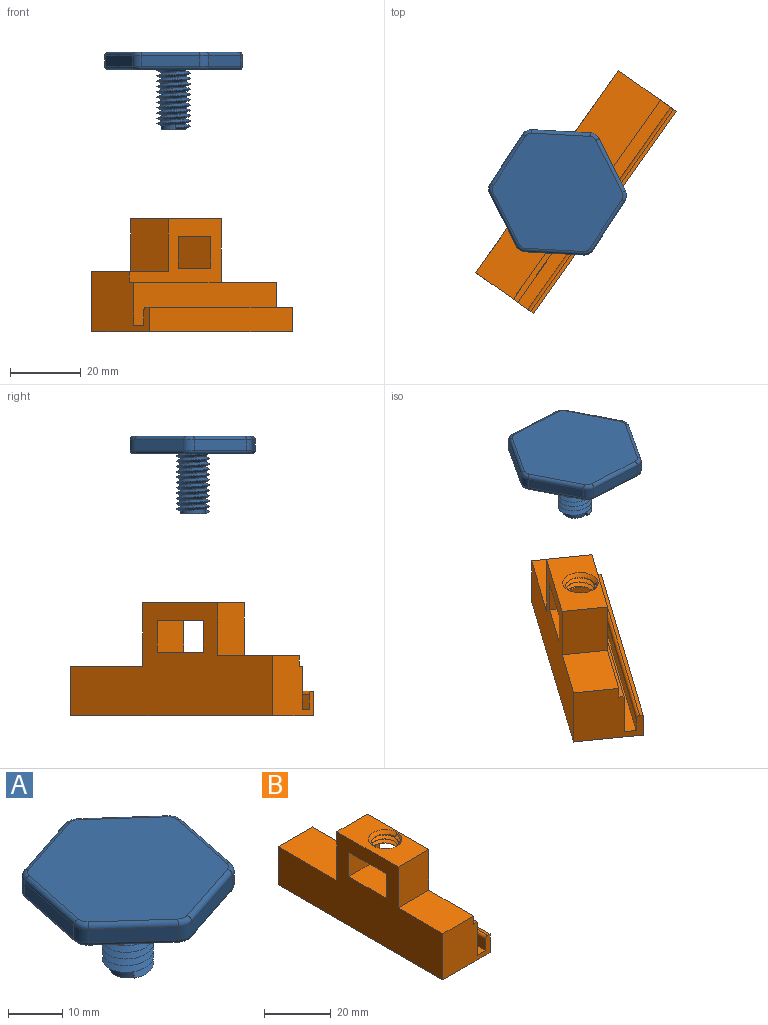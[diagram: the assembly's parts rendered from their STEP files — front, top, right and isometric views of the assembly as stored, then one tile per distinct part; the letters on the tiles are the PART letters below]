
ASSEMBLY  parts=2 mates=1
PART A: 43 faces, bbox 38.8x39.8x22.9 mm
  f0: plane 37.3x36.33mm, normal (0,0,-1), area 869mm2, adj f2,f3,f4,f13,f14,f15,f16,f17
  f1: plane 36.38x35.41mm, normal (0,0,1), area 921.4mm2, adj f19,f20,f21,f22,f23,f24,f27,f30
  f2: cylinder r=3.5mm len=17mm, axis (0,0,-1), area 1.1mm2, adj f0,f3,f4,f5,f6
  f3: bspline ~17.2x10.88mm, area 384.8mm2, adj f0,f2,f4,f6
  f4: bspline ~17.95x10.88mm, area 401.1mm2, adj f0,f2,f3,f6
  f5: plane 7x7mm, normal (0,0,-1), area 38.5mm2, adj f2
  f6: plane 1.4x1.05mm, normal (-0.87,0.5,0), area 0.8mm2, adj f2,f3,f4
  f7: plane 12.34x11.01mm, normal (-0.67,-0.75,0), area 49.6mm2, adj f15,f21,f38,f41
  f8: plane 15.71x5.18mm, normal (0.31,-0.95,0), area 49.6mm2, adj f13,f19,f35,f38
  f9: plane 16.19x3.37mm, normal (0.98,-0.2,0), area 49.6mm2, adj f14,f20,f32,f35
  f10: plane 12.34x11.01mm, normal (0.67,0.75,0), area 49.6mm2, adj f16,f22,f26,f32
  f11: plane 15.71x5.18mm, normal (-0.31,0.95,0), area 49.6mm2, adj f18,f24,f26,f29
  f12: plane 16.19x3.37mm, normal (-0.98,0.2,0), area 49.6mm2, adj f17,f23,f29,f41
  f13: cylinder r=1mm len=16.02mm, axis (-0.95,-0.31,0), area 26mm2, adj f0,f8,f34,f37
  f14: cylinder r=1mm len=16.39mm, axis (-0.2,-0.98,0), area 26mm2, adj f0,f9,f31,f34
  f15: cylinder r=1mm len=13mm, axis (-0.75,0.67,0), area 26mm2, adj f0,f7,f37,f40
  f16: cylinder r=1mm len=13mm, axis (0.75,-0.67,0), area 26mm2, adj f0,f10,f25,f31
  f17: cylinder r=1mm len=16.39mm, axis (0.2,0.98,0), area 26mm2, adj f0,f12,f28,f40
  f18: cylinder r=1mm len=16.02mm, axis (0.95,0.31,0), area 26mm2, adj f0,f11,f25,f28
  f19: cylinder r=1mm len=16.02mm, axis (0.95,0.31,0), area 26mm2, adj f1,f8,f36,f39
  f20: cylinder r=1mm len=16.39mm, axis (0.2,0.98,0), area 26mm2, adj f1,f9,f33,f36
  f21: cylinder r=1mm len=13mm, axis (0.75,-0.67,0), area 26mm2, adj f1,f7,f39,f42
  f22: cylinder r=1mm len=13mm, axis (-0.75,0.67,0), area 26mm2, adj f1,f10,f27,f33
  f23: cylinder r=1mm len=16.39mm, axis (-0.2,-0.98,0), area 26mm2, adj f1,f12,f30,f42
  f24: cylinder r=1mm len=16.02mm, axis (-0.95,-0.31,0), area 26mm2, adj f1,f11,f27,f30
  f25: torus R=2mm, axis (0,0,1), area 4.3mm2, adj f0,f16,f18,f26
  f26: cylinder r=3mm len=3mm, axis (0,0,1), area 9.4mm2, adj f10,f11,f25,f27
  f27: torus R=2mm, axis (0,0,1), area 4.3mm2, adj f1,f22,f24,f26
  f28: torus R=2mm, axis (0,0,1), area 4.3mm2, adj f0,f17,f18,f29
  f29: cylinder r=3mm len=3mm, axis (0,0,1), area 9.4mm2, adj f11,f12,f28,f30
  f30: torus R=2mm, axis (0,0,1), area 4.3mm2, adj f1,f23,f24,f29
  f31: torus R=2mm, axis (0,0,1), area 4.3mm2, adj f0,f14,f16,f32
  f32: cylinder r=3mm len=3mm, axis (0,0,1), area 9.4mm2, adj f9,f10,f31,f33
  f33: torus R=2mm, axis (0,0,1), area 4.3mm2, adj f1,f20,f22,f32
  f34: torus R=2mm, axis (0,0,1), area 4.3mm2, adj f0,f13,f14,f35
  f35: cylinder r=3mm len=3mm, axis (0,0,1), area 9.4mm2, adj f8,f9,f34,f36
  f36: torus R=2mm, axis (0,0,1), area 4.3mm2, adj f1,f19,f20,f35
  f37: torus R=2mm, axis (0,0,1), area 4.3mm2, adj f0,f13,f15,f38
  f38: cylinder r=3mm len=3mm, axis (0,0,1), area 9.4mm2, adj f7,f8,f37,f39
  f39: torus R=2mm, axis (0,0,1), area 4.3mm2, adj f1,f19,f21,f38
  f40: torus R=2mm, axis (0,0,1), area 4.3mm2, adj f0,f15,f17,f41
  f41: cylinder r=3mm len=3mm, axis (0,0,1), area 9.4mm2, adj f7,f12,f40,f42
  f42: torus R=2mm, axis (0,0,1), area 4.3mm2, adj f1,f21,f23,f41
PART B: 25 faces, bbox 20.9x70.9x32.9 mm
  f0: plane 20x14mm, normal (0,1,0), area 223.2mm2, adj f2,f8,f9,f10,f11,f12,f21,f22
  f1: plane 20x17mm, normal (0,-1,0), area 262.2mm2, adj f2,f3,f8,f9,f10,f11,f12,f19
  f2: plane 70x32mm, normal (-1,0,0), area 1361mm2, adj f0,f1,f3,f4,f5,f6,f7,f8
  f3: plane 19x13mm, normal (0,0,1), area 247mm2, adj f1,f2,f6,f19
  f4: plane 13x9mm, normal (0,-1,0), area 117mm2, adj f2,f7,f19,f23
  f5: plane 13x9mm, normal (0,1,0), area 117mm2, adj f2,f7,f19,f23
  f6: plane 15x13mm, normal (0,-1,0), area 195mm2, adj f2,f3,f14,f19
  f7: plane 16.94x13.94mm, normal (0,0,-1), area 142.1mm2, adj f2,f4,f5,f15,f16,f17,f19
  f8: plane 70x20mm, normal (0,0,-1), area 1400mm2, adj f0,f1,f2,f9
  f9: plane 70x6.95mm, normal (1,0,0), area 486.5mm2, adj f0,f1,f8,f11
  f10: plane 70x4.1mm, normal (-1,0,0), area 287mm2, adj f0,f1,f12,f22
  f11: plane 70x1mm, normal (0,0,1), area 70mm2, adj f0,f1,f9,f12
  f12: cylinder r=1mm len=70mm, axis (0,1,0), area 110mm2, adj f0,f1,f10,f11
  f13: plane 18x13mm, normal (0,1,0), area 234mm2, adj f2,f14,f19,f21
  f14: plane 26x13mm, normal (0,0,1), area 259.5mm2, adj f2,f6,f13,f19,f20
  f15: cylinder r=4mm len=8mm, axis (0,0,1), area 8mm2, adj f7,f16,f17,f18,f20
  f16: bspline ~10.42x10.42mm, area 118.9mm2, adj f7,f15,f17,f18,f20
  f17: bspline ~10.4x10.4mm, area 107.3mm2, adj f7,f15,f16,f18
  f18: plane 1.21x1.03mm, normal (0,-1,0), area 0.5mm2, adj f15,f16,f17,f20
  f19: plane 45x18mm, normal (1,0,0), area 381mm2, adj f1,f3,f4,f5,f6,f7,f13,f14
  f20: cone r=4mm half-angle=45deg, axis (0,0,1), area 32.1mm2, adj f14,f15,f16,f18
  f21: plane 70x14.5mm, normal (0,0,1), area 430mm2, adj f0,f1,f2,f13,f19,f24
  f22: plane 70x3.5mm, normal (0,0,1), area 245mm2, adj f0,f1,f10,f24
  f23: plane 16x13mm, normal (0,0,1), area 208mm2, adj f2,f4,f5,f19
  f24: plane 70x12.15mm, normal (1,0,0), area 850.5mm2, adj f0,f1,f21,f22
PLACE A rot(axis=(0,0,1),38.6deg) t=(-16.85,4.15,66.42)mm
PLACE B rot(axis=(0,0,-1),35.2deg) t=(-27.76,-18.33,9.29)mm fixed
MATE cylindrical A.f2 <-> B.f7  axis (0,0,-1) through (-16.85,4.15,66.42)mm
